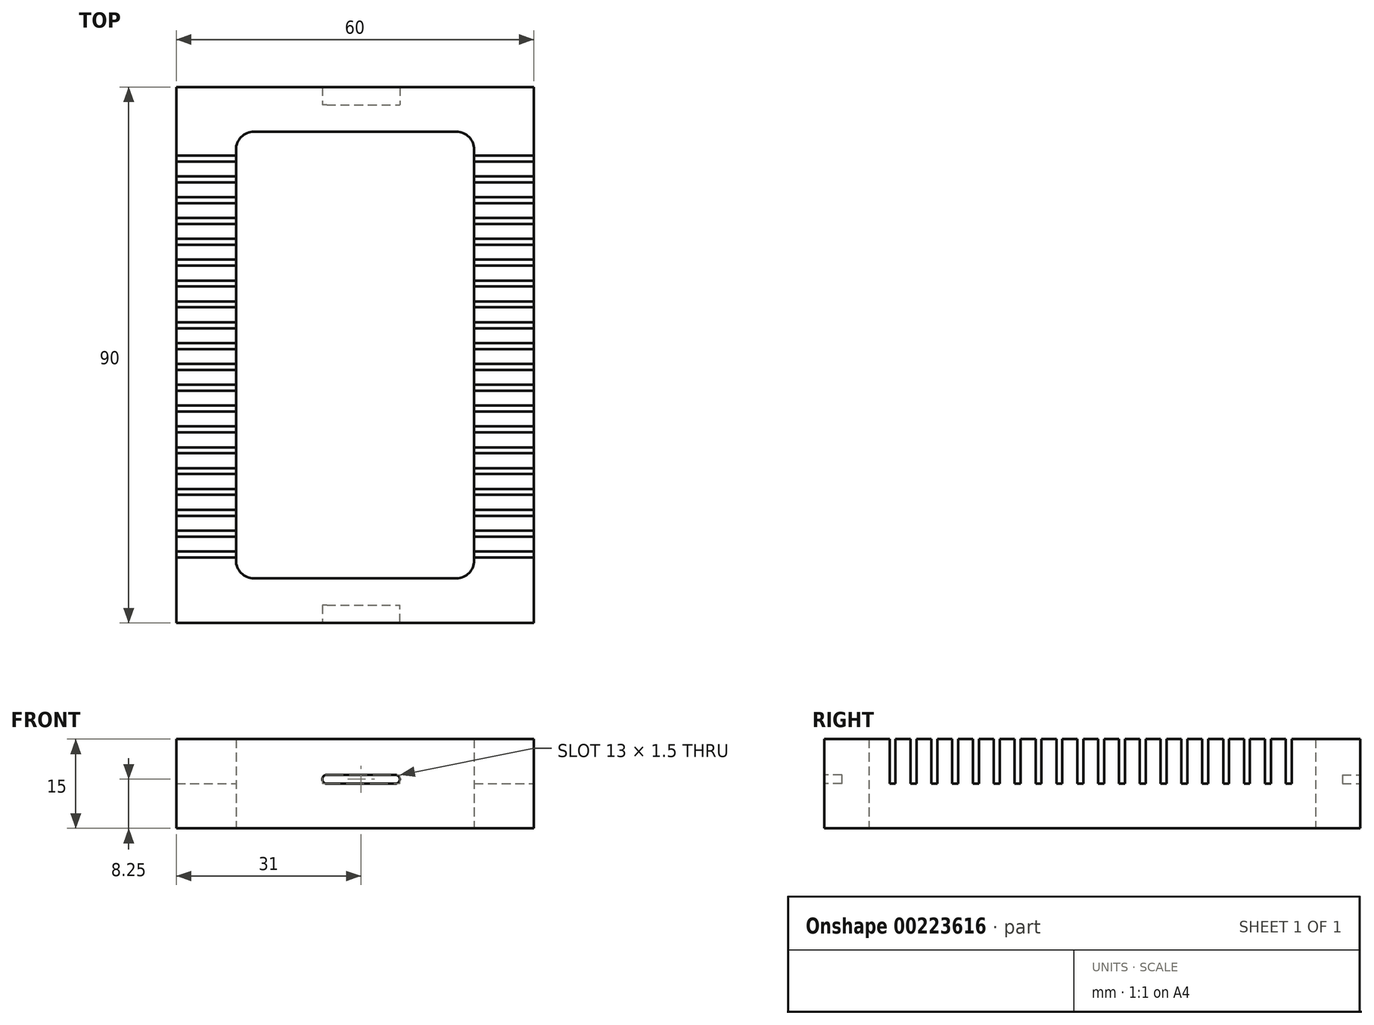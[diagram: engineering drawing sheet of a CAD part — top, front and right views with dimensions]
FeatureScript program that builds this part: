
annotation { "Feature Type Name" : "Feature", "Feature Type Description" : "" }
export const myFeature = defineFeature(function(context is Context, id is Id, definition is map)
    precondition{}
    {
        {
            var Q0;
            Q0=qCreatedBy(makeId("Top.planeOp"),FACE);
            var sketch = newSketch(context, id + "F0", { "sketchPlane" : qUnion([Q0])});
            skCircle(sketch, "E0", {"center": v(0, 0) * mm, "radius": 60 * mm, "construction": true});
            skLineSegment(sketch, "E1.bottom", {"start": v(-30, -45) * mm, "end": v(30, -45) * mm});
            skLineSegment(sketch, "E1.top", {"start": v(-30, 45) * mm, "end": v(30, 45) * mm});
            skLineSegment(sketch, "E1.left", {"start": v(-30, -45) * mm, "end": v(-30, 45) * mm});
            skLineSegment(sketch, "E1.right", {"start": v(30, -45) * mm, "end": v(30, 45) * mm});
            skLineSegment(sketch, "E2", {"start": v(-38.5, 46.02) * mm, "end": v(38.5, 46.02) * mm, "construction": true});
            skLineSegment(sketch, "E3.bottom", {"start": v(-17, 37.5) * mm, "end": v(17, 37.5) * mm});
            skLineSegment(sketch, "E3.top", {"start": v(-17, -37.5) * mm, "end": v(17, -37.5) * mm});
            skLineSegment(sketch, "E3.left", {"start": v(-20, 34.5) * mm, "end": v(-20, -34.5) * mm});
            skLineSegment(sketch, "E3.right", {"start": v(20, 34.5) * mm, "end": v(20, -34.5) * mm});
            skPoint(sketch, "E4.visualSharp", {"position": v(-20, 37.5) * mm});
            skArc(sketch, "E4.filletArc", {"start": v(-17, 37.5) * mm, "mid": v(-19.12, 36.62) * mm, "end": v(-20, 34.5) * mm});
            skPoint(sketch, "E5.visualSharp", {"position": v(20, 37.5) * mm});
            skArc(sketch, "E5.filletArc", {"start": v(20, 34.5) * mm, "mid": v(19.12, 36.62) * mm, "end": v(17, 37.5) * mm});
            skPoint(sketch, "E6.visualSharp", {"position": v(20, -37.5) * mm});
            skArc(sketch, "E6.filletArc", {"start": v(17, -37.5) * mm, "mid": v(19.12, -36.62) * mm, "end": v(20, -34.5) * mm});
            skPoint(sketch, "E7.visualSharp", {"position": v(-20, -37.5) * mm});
            skArc(sketch, "E7.filletArc", {"start": v(-20, -34.5) * mm, "mid": v(-19.12, -36.62) * mm, "end": v(-17, -37.5) * mm});
            skSolve(sketch);
        }
        {
            var Q0;
            Q0=makeQuery(id+"F0.imprint","IMPRINT",FACE,{"disambiguationData":[TD([[makeQuery(id+"F0.imprint","IMPRINT",EDGE,{"derivedFrom":sQuery(id+"F0.wireOp",EDGE,"E1.bottom")}),1.0]])]});
            extrude(context, id + "F1", {"entities" : qUnion([Q0]), "depth" : 15 * mm});
        }
        {
            var Q0;
            Q0=makeQuery(id+"F1.opExtrude","CAP_FACE",FACE,{"disambiguationData":[OSD([sQuery(id+"F0.wireOp",EDGE,"E1.bottom"),sQuery(id+"F0.wireOp",EDGE,"E1.top"),sQuery(id+"F0.wireOp",EDGE,"E1.left"),sQuery(id+"F0.wireOp",EDGE,"E1.right"),sQuery(id+"F0.wireOp",EDGE,"E3.bottom"),sQuery(id+"F0.wireOp",EDGE,"E3.top"),sQuery(id+"F0.wireOp",EDGE,"E3.left"),sQuery(id+"F0.wireOp",EDGE,"E3.right"),sQuery(id+"F0.wireOp",EDGE,"E4.filletArc"),sQuery(id+"F0.wireOp",EDGE,"E5.filletArc"),sQuery(id+"F0.wireOp",EDGE,"E6.filletArc"),sQuery(id+"F0.wireOp",EDGE,"E7.filletArc")])],"isStart":false});
            var sketch = newSketch(context, id + "F2", { "sketchPlane" : qUnion([Q0])});
            skLineSegment(sketch, "E8.bottom", {"start": v(-30, -34) * mm, "end": v(30, -34) * mm});
            skLineSegment(sketch, "E8.top", {"start": v(-30, -33) * mm, "end": v(30, -33) * mm});
            skLineSegment(sketch, "E8.left", {"start": v(-30, -34) * mm, "end": v(-30, -33) * mm});
            skLineSegment(sketch, "E8.right", {"start": v(30, -34) * mm, "end": v(30, -33) * mm});
            skLineSegment(sketch, "E9.0.1.0", {"start": v(-30, -29.5) * mm, "end": v(30, -29.5) * mm});
            skLineSegment(sketch, "E9.0.1.1", {"start": v(-30, -30.5) * mm, "end": v(30, -30.5) * mm});
            skLineSegment(sketch, "E9.0.1.2", {"start": v(30, -30.5) * mm, "end": v(30, -29.5) * mm});
            skLineSegment(sketch, "E9.0.1.3", {"start": v(-30, -30.5) * mm, "end": v(-30, -29.5) * mm});
            skLineSegment(sketch, "E9.0.2.0", {"start": v(-30, -26) * mm, "end": v(30, -26) * mm});
            skLineSegment(sketch, "E9.0.2.1", {"start": v(-30, -27) * mm, "end": v(30, -27) * mm});
            skLineSegment(sketch, "E9.0.2.2", {"start": v(30, -27) * mm, "end": v(30, -26) * mm});
            skLineSegment(sketch, "E9.0.2.3", {"start": v(-30, -27) * mm, "end": v(-30, -26) * mm});
            skLineSegment(sketch, "E9.0.3.0", {"start": v(-30, -22.5) * mm, "end": v(30, -22.5) * mm});
            skLineSegment(sketch, "E9.0.3.1", {"start": v(-30, -23.5) * mm, "end": v(30, -23.5) * mm});
            skLineSegment(sketch, "E9.0.3.2", {"start": v(30, -23.5) * mm, "end": v(30, -22.5) * mm});
            skLineSegment(sketch, "E9.0.3.3", {"start": v(-30, -23.5) * mm, "end": v(-30, -22.5) * mm});
            skLineSegment(sketch, "E9.0.4.0", {"start": v(-30, -19) * mm, "end": v(30, -19) * mm});
            skLineSegment(sketch, "E9.0.4.1", {"start": v(-30, -20) * mm, "end": v(30, -20) * mm});
            skLineSegment(sketch, "E9.0.4.2", {"start": v(30, -20) * mm, "end": v(30, -19) * mm});
            skLineSegment(sketch, "E9.0.4.3", {"start": v(-30, -20) * mm, "end": v(-30, -19) * mm});
            skLineSegment(sketch, "E9.0.5.0", {"start": v(-30, -15.5) * mm, "end": v(30, -15.5) * mm});
            skLineSegment(sketch, "E9.0.5.1", {"start": v(-30, -16.5) * mm, "end": v(30, -16.5) * mm});
            skLineSegment(sketch, "E9.0.5.2", {"start": v(30, -16.5) * mm, "end": v(30, -15.5) * mm});
            skLineSegment(sketch, "E9.0.5.3", {"start": v(-30, -16.5) * mm, "end": v(-30, -15.5) * mm});
            skLineSegment(sketch, "E9.0.6.0", {"start": v(-30, -12) * mm, "end": v(30, -12) * mm});
            skLineSegment(sketch, "E9.0.6.1", {"start": v(-30, -13) * mm, "end": v(30, -13) * mm});
            skLineSegment(sketch, "E9.0.6.2", {"start": v(30, -13) * mm, "end": v(30, -12) * mm});
            skLineSegment(sketch, "E9.0.6.3", {"start": v(-30, -13) * mm, "end": v(-30, -12) * mm});
            skLineSegment(sketch, "E9.0.7.0", {"start": v(-30, -8.5) * mm, "end": v(30, -8.5) * mm});
            skLineSegment(sketch, "E9.0.7.1", {"start": v(-30, -9.5) * mm, "end": v(30, -9.5) * mm});
            skLineSegment(sketch, "E9.0.7.2", {"start": v(30, -9.5) * mm, "end": v(30, -8.5) * mm});
            skLineSegment(sketch, "E9.0.7.3", {"start": v(-30, -9.5) * mm, "end": v(-30, -8.5) * mm});
            skLineSegment(sketch, "E9.0.8.0", {"start": v(-30, -5) * mm, "end": v(30, -5) * mm});
            skLineSegment(sketch, "E9.0.8.1", {"start": v(-30, -6) * mm, "end": v(30, -6) * mm});
            skLineSegment(sketch, "E9.0.8.2", {"start": v(30, -6) * mm, "end": v(30, -5) * mm});
            skLineSegment(sketch, "E9.0.8.3", {"start": v(-30, -6) * mm, "end": v(-30, -5) * mm});
            skLineSegment(sketch, "E9.0.9.0", {"start": v(-30, -1.5) * mm, "end": v(30, -1.5) * mm});
            skLineSegment(sketch, "E9.0.9.1", {"start": v(-30, -2.5) * mm, "end": v(30, -2.5) * mm});
            skLineSegment(sketch, "E9.0.9.2", {"start": v(30, -2.5) * mm, "end": v(30, -1.5) * mm});
            skLineSegment(sketch, "E9.0.9.3", {"start": v(-30, -2.5) * mm, "end": v(-30, -1.5) * mm});
            skLineSegment(sketch, "E9.0.10.0", {"start": v(-30, 2) * mm, "end": v(30, 2) * mm});
            skLineSegment(sketch, "E9.0.10.1", {"start": v(-30, 1) * mm, "end": v(30, 1) * mm});
            skLineSegment(sketch, "E9.0.10.2", {"start": v(30, 1) * mm, "end": v(30, 2) * mm});
            skLineSegment(sketch, "E9.0.10.3", {"start": v(-30, 1) * mm, "end": v(-30, 2) * mm});
            skLineSegment(sketch, "E9.0.11.0", {"start": v(-30, 5.5) * mm, "end": v(30, 5.5) * mm});
            skLineSegment(sketch, "E9.0.11.1", {"start": v(-30, 4.5) * mm, "end": v(30, 4.5) * mm});
            skLineSegment(sketch, "E9.0.11.2", {"start": v(30, 4.5) * mm, "end": v(30, 5.5) * mm});
            skLineSegment(sketch, "E9.0.11.3", {"start": v(-30, 4.5) * mm, "end": v(-30, 5.5) * mm});
            skLineSegment(sketch, "E9.0.12.0", {"start": v(-30, 9) * mm, "end": v(30, 9) * mm});
            skLineSegment(sketch, "E9.0.12.1", {"start": v(-30, 8) * mm, "end": v(30, 8) * mm});
            skLineSegment(sketch, "E9.0.12.2", {"start": v(30, 8) * mm, "end": v(30, 9) * mm});
            skLineSegment(sketch, "E9.0.12.3", {"start": v(-30, 8) * mm, "end": v(-30, 9) * mm});
            skLineSegment(sketch, "E9.0.13.0", {"start": v(-30, 12.5) * mm, "end": v(30, 12.5) * mm});
            skLineSegment(sketch, "E9.0.13.1", {"start": v(-30, 11.5) * mm, "end": v(30, 11.5) * mm});
            skLineSegment(sketch, "E9.0.13.2", {"start": v(30, 11.5) * mm, "end": v(30, 12.5) * mm});
            skLineSegment(sketch, "E9.0.13.3", {"start": v(-30, 11.5) * mm, "end": v(-30, 12.5) * mm});
            skLineSegment(sketch, "E9.0.14.0", {"start": v(-30, 16) * mm, "end": v(30, 16) * mm});
            skLineSegment(sketch, "E9.0.14.1", {"start": v(-30, 15) * mm, "end": v(30, 15) * mm});
            skLineSegment(sketch, "E9.0.14.2", {"start": v(30, 15) * mm, "end": v(30, 16) * mm});
            skLineSegment(sketch, "E9.0.14.3", {"start": v(-30, 15) * mm, "end": v(-30, 16) * mm});
            skLineSegment(sketch, "E9.0.15.0", {"start": v(-30, 19.5) * mm, "end": v(30, 19.5) * mm});
            skLineSegment(sketch, "E9.0.15.1", {"start": v(-30, 18.5) * mm, "end": v(30, 18.5) * mm});
            skLineSegment(sketch, "E9.0.15.2", {"start": v(30, 18.5) * mm, "end": v(30, 19.5) * mm});
            skLineSegment(sketch, "E9.0.15.3", {"start": v(-30, 18.5) * mm, "end": v(-30, 19.5) * mm});
            skLineSegment(sketch, "E9.0.16.0", {"start": v(-30, 23) * mm, "end": v(30, 23) * mm});
            skLineSegment(sketch, "E9.0.16.1", {"start": v(-30, 22) * mm, "end": v(30, 22) * mm});
            skLineSegment(sketch, "E9.0.16.2", {"start": v(30, 22) * mm, "end": v(30, 23) * mm});
            skLineSegment(sketch, "E9.0.16.3", {"start": v(-30, 22) * mm, "end": v(-30, 23) * mm});
            skLineSegment(sketch, "E9.0.17.0", {"start": v(-30, 26.5) * mm, "end": v(30, 26.5) * mm});
            skLineSegment(sketch, "E9.0.17.1", {"start": v(-30, 25.5) * mm, "end": v(30, 25.5) * mm});
            skLineSegment(sketch, "E9.0.17.2", {"start": v(30, 25.5) * mm, "end": v(30, 26.5) * mm});
            skLineSegment(sketch, "E9.0.17.3", {"start": v(-30, 25.5) * mm, "end": v(-30, 26.5) * mm});
            skLineSegment(sketch, "E9.0.18.0", {"start": v(-30, 30) * mm, "end": v(30, 30) * mm});
            skLineSegment(sketch, "E9.0.18.1", {"start": v(-30, 29) * mm, "end": v(30, 29) * mm});
            skLineSegment(sketch, "E9.0.18.2", {"start": v(30, 29) * mm, "end": v(30, 30) * mm});
            skLineSegment(sketch, "E9.0.18.3", {"start": v(-30, 29) * mm, "end": v(-30, 30) * mm});
            skLineSegment(sketch, "E9.0.19.0", {"start": v(-30, 33.5) * mm, "end": v(30, 33.5) * mm});
            skLineSegment(sketch, "E9.0.19.1", {"start": v(-30, 32.5) * mm, "end": v(30, 32.5) * mm});
            skLineSegment(sketch, "E9.0.19.2", {"start": v(30, 32.5) * mm, "end": v(30, 33.5) * mm});
            skLineSegment(sketch, "E9.0.19.3", {"start": v(-30, 32.5) * mm, "end": v(-30, 33.5) * mm});
            skLineSegment(sketch, "E9.direction1", {"start": v(-30, -33) * mm, "end": v(-5, -33) * mm, "construction": true});
            skLineSegment(sketch, "E9.direction2", {"start": v(-30, -33) * mm, "end": v(-30, -29.5) * mm, "construction": true});
            skSolve(sketch);
        }
        {
            var Q0;
            Q0 = qSketchRegion(id + "F2", true);
            extrude(context, id + "F3", {"entities" : qUnion([Q0]), "operationType" : NewBodyOperationType.REMOVE, "oppositeDirection" : true, "depth" : 7.5 * mm});
        }
        {
            var Q0;
            Q0=makeQuery(id+"F1.opExtrude","SWEPT_FACE",FACE,{"disambiguationData":[OSD([sQuery(id+"F0.wireOp",EDGE,"E1.bottom")])]});
            var sketch = newSketch(context, id + "F4", { "sketchPlane" : qUnion([Q0])});
            skLineSegment(sketch, "E10.bottom", {"start": v(-5.5, 7.5) * mm, "end": v(7.5, 7.5) * mm});
            skLineSegment(sketch, "E10.top", {"start": v(-5.5, 9) * mm, "end": v(7.5, 9) * mm});
            skLineSegment(sketch, "E10.left", {"start": v(-5.5, 7.5) * mm, "end": v(-5.5, 9) * mm});
            skLineSegment(sketch, "E10.right", {"start": v(7.5, 7.5) * mm, "end": v(7.5, 9) * mm});
            skSolve(sketch);
        }
        {
            var Q0;
            Q0 = qSketchRegion(id + "F4", true);
            extrude(context, id + "F5", {"entities" : qUnion([Q0]), "operationType" : NewBodyOperationType.REMOVE, "oppositeDirection" : true, "depth" : 3 * mm});
        }
        {
            var Q0;
            Q0=makeQuery(id+"F5.boolean.opBoolean","COPY",EDGE,{"derivedFrom":makeQuery(id+"F5.opExtrude","SWEPT_EDGE",EDGE,{"disambiguationData":[OSD([sQuery(id+"F4.wireOp",EDGE,"E10.bottom"),sQuery(id+"F4.wireOp",EDGE,"E10.left")])]})});
            var Q1;
            Q1=makeQuery(id+"F5.boolean.opBoolean","COPY",EDGE,{"derivedFrom":makeQuery(id+"F5.opExtrude","SWEPT_EDGE",EDGE,{"disambiguationData":[OSD([sQuery(id+"F4.wireOp",EDGE,"E10.top"),sQuery(id+"F4.wireOp",EDGE,"E10.left")])]})});
            var Q2;
            Q2=makeQuery(id+"F5.boolean.opBoolean","COPY",EDGE,{"derivedFrom":makeQuery(id+"F5.opExtrude","SWEPT_EDGE",EDGE,{"disambiguationData":[OSD([sQuery(id+"F4.wireOp",EDGE,"E10.bottom"),sQuery(id+"F4.wireOp",EDGE,"E10.right")])]})});
            var Q3;
            Q3=makeQuery(id+"F5.boolean.opBoolean","COPY",EDGE,{"derivedFrom":makeQuery(id+"F5.opExtrude","SWEPT_EDGE",EDGE,{"disambiguationData":[OSD([sQuery(id+"F4.wireOp",EDGE,"E10.top"),sQuery(id+"F4.wireOp",EDGE,"E10.right")])]})});
            fillet(context, id + "F6", {"entities" : qUnion([Q0, Q1, Q2, Q3]), "radius" : .75 * mm, "tangentPropagation" : true, "allowEdgeOverflow" : false});
        }
        {
            var Q0;
            Q0=makeQuery(id+"F1.opExtrude","SWEPT_FACE",FACE,{"disambiguationData":[OSD([sQuery(id+"F0.wireOp",EDGE,"E1.top")])]});
            var sketch = newSketch(context, id + "F7", { "sketchPlane" : qUnion([Q0])});
            skLineSegment(sketch, "E11.bottom", {"start": v(5.5, 9) * mm, "end": v(-7.5, 9) * mm});
            skLineSegment(sketch, "E11.top", {"start": v(5.5, 7.5) * mm, "end": v(-7.5, 7.5) * mm});
            skLineSegment(sketch, "E11.left", {"start": v(5.5, 9) * mm, "end": v(5.5, 7.5) * mm});
            skLineSegment(sketch, "E11.right", {"start": v(-7.5, 9) * mm, "end": v(-7.5, 7.5) * mm});
            skSolve(sketch);
        }
        {
            var Q0;
            Q0 = qSketchRegion(id + "F7", true);
            extrude(context, id + "F8", {"entities" : qUnion([Q0]), "operationType" : NewBodyOperationType.REMOVE, "oppositeDirection" : true, "depth" : 3 * mm});
        }
        {
            var Q0;
            Q0=makeQuery(id+"F8.boolean.opBoolean","COPY",EDGE,{"derivedFrom":makeQuery(id+"F8.opExtrude","SWEPT_EDGE",EDGE,{"disambiguationData":[OSD([sQuery(id+"F7.wireOp",EDGE,"E11.top"),sQuery(id+"F7.wireOp",EDGE,"E11.left")])]})});
            var Q1;
            Q1=makeQuery(id+"F8.boolean.opBoolean","COPY",EDGE,{"derivedFrom":makeQuery(id+"F8.opExtrude","SWEPT_EDGE",EDGE,{"disambiguationData":[OSD([sQuery(id+"F7.wireOp",EDGE,"E11.bottom"),sQuery(id+"F7.wireOp",EDGE,"E11.left")])]})});
            var Q2;
            Q2=makeQuery(id+"F8.boolean.opBoolean","COPY",EDGE,{"derivedFrom":makeQuery(id+"F8.opExtrude","SWEPT_EDGE",EDGE,{"disambiguationData":[OSD([sQuery(id+"F7.wireOp",EDGE,"E11.bottom"),sQuery(id+"F7.wireOp",EDGE,"E11.right")])]})});
            var Q3;
            Q3=makeQuery(id+"F8.boolean.opBoolean","COPY",EDGE,{"derivedFrom":makeQuery(id+"F8.opExtrude","SWEPT_EDGE",EDGE,{"disambiguationData":[OSD([sQuery(id+"F7.wireOp",EDGE,"E11.top"),sQuery(id+"F7.wireOp",EDGE,"E11.right")])]})});
            fillet(context, id + "F9", {"entities" : qUnion([Q0, Q1, Q2, Q3]), "radius" : .75 * mm, "tangentPropagation" : true, "allowEdgeOverflow" : false});
        }
    });
